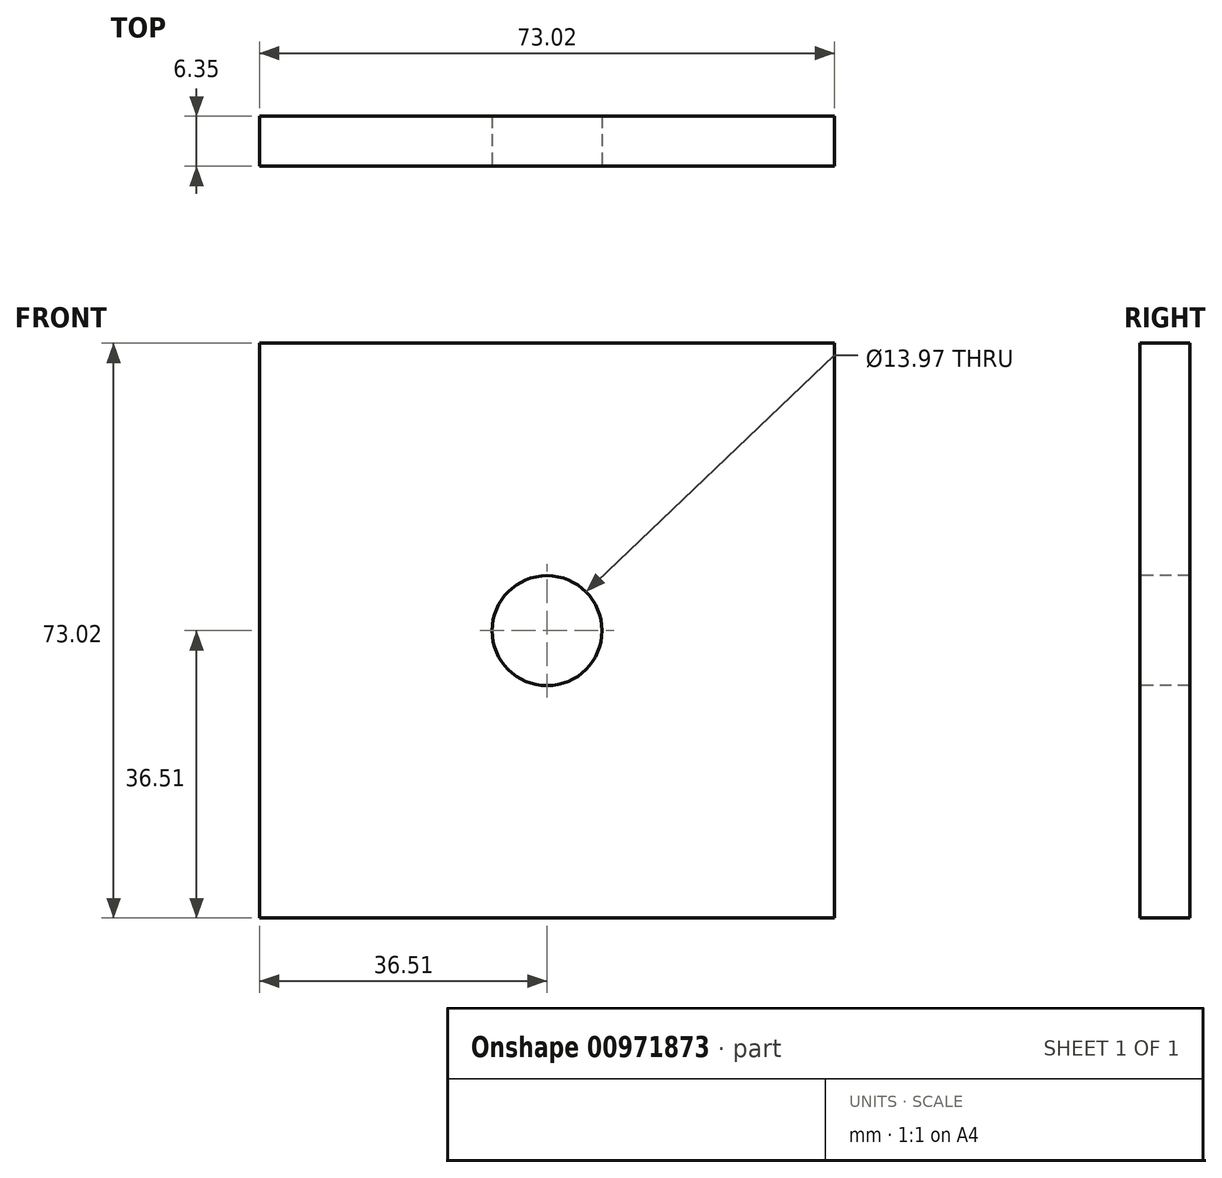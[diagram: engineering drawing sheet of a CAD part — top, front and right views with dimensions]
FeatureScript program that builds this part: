
annotation { "Feature Type Name" : "Feature", "Feature Type Description" : "" }
export const myFeature = defineFeature(function(context is Context, id is Id, definition is map)
    precondition{}
    {
        {
            var Q0;
            Q0=qCreatedBy(makeId("Front.planeOp"),FACE);
            var sketch = newSketch(context, id + "F0", { "sketchPlane" : qUnion([Q0])});
            skLineSegment(sketch, "E0.bottom", {"start": v(-36.51, 36.51) * mm, "end": v(36.51, 36.51) * mm});
            skLineSegment(sketch, "E0.top", {"start": v(-36.51, -36.51) * mm, "end": v(36.51, -36.51) * mm});
            skLineSegment(sketch, "E0.left", {"start": v(-36.51, 36.51) * mm, "end": v(-36.51, -36.51) * mm});
            skLineSegment(sketch, "E0.right", {"start": v(36.51, 36.51) * mm, "end": v(36.51, -36.51) * mm});
            skPoint(sketch, "E0.middle", {"position": v(0, 0) * mm});
            skCircle(sketch, "E1", {"center": v(0, 0) * mm, "radius": 6.99 * mm});
            skSolve(sketch);
        }
        {
            var Q0;
            Q0 = qSketchRegion(id + "F0", true);
            extrude(context, id + "F1", {"entities" : qUnion([Q0]), "oppositeDirection" : true, "depth" : 6.35 * mm, "offsetDistance" : 25.4 * mm});
        }
    });
